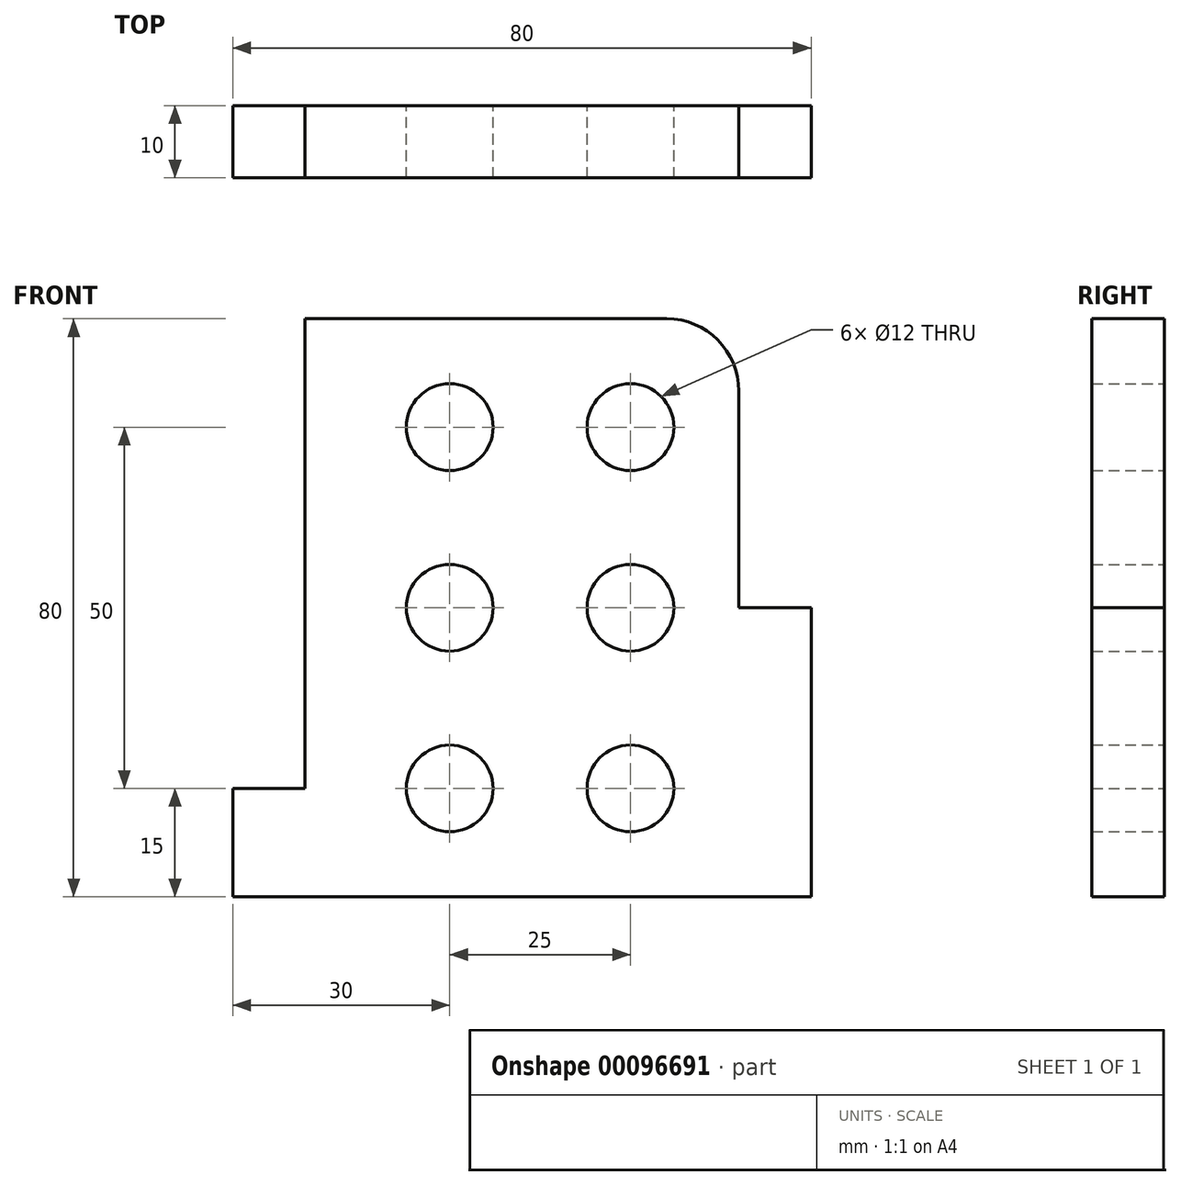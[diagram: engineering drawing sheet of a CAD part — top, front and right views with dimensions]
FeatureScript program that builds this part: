
annotation { "Feature Type Name" : "Feature", "Feature Type Description" : "" }
export const myFeature = defineFeature(function(context is Context, id is Id, definition is map)
    precondition{}
    {
        {
            var Q0;
            Q0=qCreatedBy(makeId("Front.planeOp"),FACE);
            var sketch = newSketch(context, id + "F0", { "sketchPlane" : qUnion([Q0])});
            skLineSegment(sketch, "E0", {"start": v(0, 0) * mm, "end": v(0, 15) * mm});
            skLineSegment(sketch, "E1", {"start": v(0, 15) * mm, "end": v(10, 15) * mm});
            skLineSegment(sketch, "E2", {"start": v(10, 15) * mm, "end": v(10, 80) * mm});
            skLineSegment(sketch, "E3", {"start": v(70, 40) * mm, "end": v(80, 40) * mm});
            skLineSegment(sketch, "E4", {"start": v(80, 40) * mm, "end": v(80, 0) * mm});
            skLineSegment(sketch, "E5", {"start": v(80, 0) * mm, "end": v(0, 0) * mm});
            skLineSegment(sketch, "E6", {"start": v(70, 40) * mm, "end": v(70, 70) * mm});
            skLineSegment(sketch, "E7", {"start": v(10, 80) * mm, "end": v(60, 80) * mm});
            skLineSegment(sketch, "E8", {"start": v(10, 15) * mm, "end": v(80, 15) * mm, "construction": true});
            skLineSegment(sketch, "E9", {"start": v(10, 40) * mm, "end": v(70, 40) * mm, "construction": true});
            skLineSegment(sketch, "E10", {"start": v(70, 65) * mm, "end": v(10, 65) * mm, "construction": true});
            skCircle(sketch, "E11", {"center": v(30, 65) * mm, "radius": 6 * mm});
            skCircle(sketch, "E12", {"center": v(55, 65) * mm, "radius": 6 * mm});
            skCircle(sketch, "E13", {"center": v(30, 40) * mm, "radius": 6 * mm});
            skCircle(sketch, "E14", {"center": v(55, 40) * mm, "radius": 6 * mm});
            skCircle(sketch, "E15", {"center": v(30, 15) * mm, "radius": 6 * mm});
            skCircle(sketch, "E16", {"center": v(55, 15) * mm, "radius": 6 * mm});
            skLineSegment(sketch, "E17", {"start": v(30, 80) * mm, "end": v(30, 0) * mm, "construction": true});
            skLineSegment(sketch, "E18", {"start": v(55, 80) * mm, "end": v(55, 0) * mm, "construction": true});
            skArc(sketch, "E19", {"start": v(60, 80) * mm, "mid": v(67.07, 77.07) * mm, "end": v(70, 70) * mm});
            skSolve(sketch);
        }
        {
            var Q0;
            Q0 = qSketchRegion(id + "F0", true);
            extrude(context, id + "F1", {"entities" : qUnion([Q0]), "depth" : 10 * mm});
        }
    });
